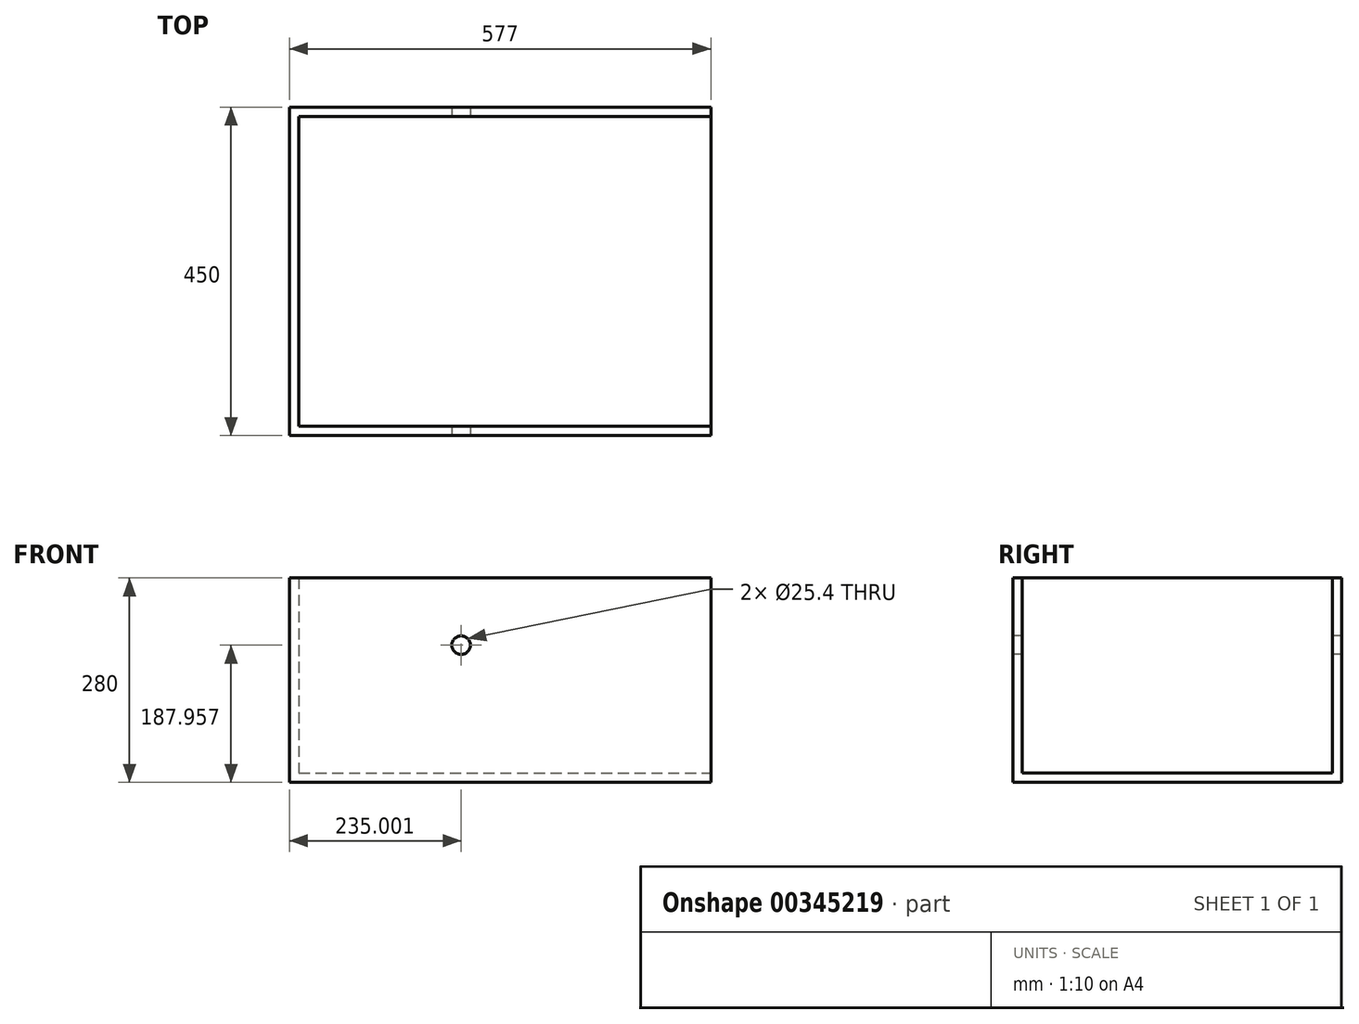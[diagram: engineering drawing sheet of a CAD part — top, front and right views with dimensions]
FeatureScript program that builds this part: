
annotation { "Feature Type Name" : "Feature", "Feature Type Description" : "" }
export const myFeature = defineFeature(function(context is Context, id is Id, definition is map)
    precondition{}
    {
        {
            var Q0;
            Q0=qCreatedBy(makeId("Front.planeOp"),FACE);
            var sketch = newSketch(context, id + "F0", { "sketchPlane" : qUnion([Q0])});
            skLineSegment(sketch, "E0.bottom", {"start": v(-134.38, 132.7) * mm, "end": v(315.62, 132.7) * mm});
            skLineSegment(sketch, "E0.top", {"start": v(-134.38, -147.3) * mm, "end": v(315.62, -147.3) * mm});
            skLineSegment(sketch, "E0.left", {"start": v(-134.38, 132.7) * mm, "end": v(-134.38, -147.3) * mm});
            skLineSegment(sketch, "E0.right", {"start": v(315.62, 132.7) * mm, "end": v(315.62, -147.3) * mm});
            skPoint(sketch, "E0.middle", {"position": v(90.62, -7.3) * mm});
            skSolve(sketch);
        }
        {
            var Q0;
            Q0=makeQuery(id+"F0.imprint","IMPRINT",FACE,{"disambiguationData":[TD([[makeQuery(id+"F0.imprint","IMPRINT",EDGE,{"derivedFrom":sQuery(id+"F0.wireOp",EDGE,"E0.bottom")}),-1.0]])]});
            extrude(context, id + "F1", {"entities" : qUnion([Q0]), "endBound" : BoundingType.SYMMETRIC, "depth" : 450 * mm});
        }
        {
            var Q0;
            Q0=makeQuery(id+"F1.opExtrude","SWEPT_FACE",FACE,{"disambiguationData":[OSD([sQuery(id+"F0.wireOp",EDGE,"E0.bottom")])]});
            shell(context, id + "F2", {"entities" : qUnion([Q0]), "thickness" : 12.7 * mm});
        }
        {
            var Q0;
            Q0=makeQuery(id+"F1.opExtrude","CAP_FACE",FACE,{"disambiguationData":[OSD([sQuery(id+"F0.wireOp",EDGE,"E0.bottom"),sQuery(id+"F0.wireOp",EDGE,"E0.top"),sQuery(id+"F0.wireOp",EDGE,"E0.left"),sQuery(id+"F0.wireOp",EDGE,"E0.right")])],"isStart":false});
            var sketch = newSketch(context, id + "F3", { "sketchPlane" : qUnion([Q0])});
            skCircle(sketch, "E1", {"center": v(100.62, 40.67) * mm, "radius": 12.7 * mm});
            skSolve(sketch);
        }
        {
            var Q0;
            Q0=makeQuery(id+"F3.imprint","IMPRINT",FACE,{"disambiguationData":[TD([[makeQuery(id+"F3.imprint","IMPRINT",EDGE,{"derivedFrom":sQuery(id+"F3.wireOp",EDGE,"E1")}),1.0]])]});
            extrude(context, id + "F4", {"entities" : qUnion([Q0]), "operationType" : NewBodyOperationType.REMOVE, "endBound" : BoundingType.THROUGH_ALL, "oppositeDirection" : true, "depth" : 25.4 * mm});
        }
        {
            var Q0;
            Q0=makeQuery(id+"F1.opExtrude","SWEPT_FACE",FACE,{"disambiguationData":[OSD([sQuery(id+"F0.wireOp",EDGE,"E0.right")])]});
            var sketch = newSketch(context, id + "F5", { "sketchPlane" : qUnion([Q0])});
            skLineSegment(sketch, "E2.bottom", {"start": v(-225, 132.7) * mm, "end": v(225, 132.7) * mm});
            skLineSegment(sketch, "E2.top", {"start": v(-225, -147.3) * mm, "end": v(225, -147.3) * mm});
            skLineSegment(sketch, "E2.left", {"start": v(-225, 132.7) * mm, "end": v(-225, -147.3) * mm});
            skLineSegment(sketch, "E2.right", {"start": v(225, 132.7) * mm, "end": v(225, -147.3) * mm});
            skSolve(sketch);
        }
        {
            var Q0;
            Q0 = qSketchRegion(id + "F5", true);
            extrude(context, id + "F6", {"entities" : qUnion([Q0]), "operationType" : NewBodyOperationType.ADD, "depth" : 127 * mm});
        }
        {
            var Q0;
            Q0=makeQuery(id+"F2.opShell","OFFSET_FACE",FACE,{"disambiguationData":[OSD([sQuery(id+"F0.wireOp",EDGE,"E0.right")])]});
            var sketch = newSketch(context, id + "F7", { "sketchPlane" : qUnion([Q0])});
            skLineSegment(sketch, "E3.bottom", {"start": v(-212.3, -134.6) * mm, "end": v(212.3, -134.6) * mm});
            skLineSegment(sketch, "E3.top", {"start": v(-212.3, 132.7) * mm, "end": v(212.3, 132.7) * mm});
            skLineSegment(sketch, "E3.left", {"start": v(-212.3, -134.6) * mm, "end": v(-212.3, 132.7) * mm});
            skLineSegment(sketch, "E3.right", {"start": v(212.3, -134.6) * mm, "end": v(212.3, 132.7) * mm});
            skSolve(sketch);
        }
        {
            var Q0;
            Q0 = qSketchRegion(id + "F7", true);
            extrude(context, id + "F8", {"entities" : qUnion([Q0]), "operationType" : NewBodyOperationType.REMOVE, "endBound" : BoundingType.THROUGH_ALL, "oppositeDirection" : true, "depth" : 25.4 * mm});
        }
    });
